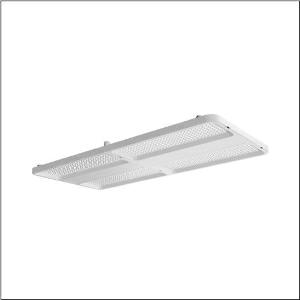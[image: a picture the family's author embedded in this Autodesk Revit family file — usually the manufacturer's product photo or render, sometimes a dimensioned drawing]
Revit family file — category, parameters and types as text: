
# Revit family: highbay_21_maxi_52hn11db4qda02
name_source: partatom
category: Lighting Fixtures
units: mm (PartAtom-declared; Revit-internal decimal feet)

## family parameters
Cut with Voids When Loaded = No
Host = Face
Light Source = No
Part Type = Normal
Room Calculation Point = No
Round Connector Dimension = Use Diameter
Shared = No

## types (1)
- --- (1 x LED, 38000 lm, 198.2 W, 4000K)
    Apparent Load = 198 VA
    CIE Flux Codes = 89 97 99 100 100
    Color Rendering = 80
    Color Temperature = 4000K
    Default Elevation = 1800 mm
    Description = high bay luminaire Highbay 21 maxi; direct symmetric narrow distribution, light control with lens of PMMA; UGR ≤ 19 (X = 4H | Y = 8H | S = 0.25H | reflection values 70/50/20); luminous flux: 38.000lm; light colour: 840, colour temperature: 4000K, MacAdam ≤ 3 SDCM (initial), colour rendering: CRI > 80; luminous efficacy: 191,7lm/W; rated service life: 75.000h (L80) at AT= ta max; control: Bluetooth Mesh; for wireless networking: Node luminaire for setting up a local control solution without a higher-level application controller, intelligence completely in the luminaire; no control line such as DALI between the Node multi-sensor luminaires and Nodes is required, wireless integration of other Node luminaires and Node multi-sensor luminaires into the network is possible; number of Node luminaires in the project can be expanded as required, network sizes > 300 Nodes can be realized; can also be connected to lighting or building automation via various gateways upon request; integrated DALI2 ECG provides luminaire data (according to IEC62386, Part 251), energy data (Part 252), and monitoring and analytics data (Part 253) to higher-level systems for further processing; luminaire connection: terminal, 5-pole, max. 2.5mm² (cable entry for one cable, Ø 8.5..16mm); mains connection: 230..240V, AC 50/60Hz; connected load: 198,2W; protection rating (complete): IP66; insulation class (complete): insulation class I (protective earthing); protection symbol: D; impact resistance: IK08; certification: CE, UKCA; internal wiring halogen-free; luminaire LABS conformity tested according to VDMA 24364:2018-05; Suitable for use in the food industry according to the specifications of IFS-Food, HACCP and/or BRC; housing frame of high-performance plastic PA6, matt traffic white (RAL 9016); cover of PMMA; dimension (LxWxH): 946 x 442 x 72mm; permissible operating ambient temperature: -20..+40°C (reducing of maximum allowable ambient temperature of 5°C with ceiling mounting); packaging unit: 1 piece; (delivery without accessories; please order mounting accessories separately)
    Height = 72 mm  [stored 0.23622 ft]
    Lamp = 1 x LED
    Lamp Light Flux = 38000 lm
    Lamp Power = 198.2 W
    Lamp count = 1
    Length = 946 mm
    Luminous efficacy = 192 lm/W
    Manufacturer = Siteco
    ModVariant = No
    Model = 52HN11DB4QDA02
    Mounting Place = Ceiling
    Mounting Type = Pendant
    Number of Poles = 1
    OnlyDefault = Yes
    Power Factor = 1
    Product Name = Highbay 21 maxi
    Product group = high bay luminaire
    ProductGroupID = 902
    Protection Class = Protection class I
    Protection Degree = IP 66
    RLX_Detail_Level = 1
    RLX_Emergency_Light_Flux = 0 lm
    RLX_Emergency_Type = 0
    RLX_Emergency_Type_DB = No
    RlxData = <blob elided: 128609 chars, md5=8ff6dd8f>
    Socket = socket
    Standby Power = 0 W
    System Light Flux = 38001 lm
    System Power = 198 W
    Type Comments = factory setting: luminous flux: 100 % | dim-lin: 254 | 918 mA
    Type Image = l_1363244.jpg
    URL = http://relux.com
    VarID = @adj_012491
    Voltage = 0 V
    Weight = 0.00 kg
    Width = 442 mm

note: [stored X ft] marks values corroborated as IEEE doubles in the binary element streams (Revit-internal decimal feet)

## geometry (parser evidence)
native form markers: Blend x4, Sweep x10
no freeform markers — native parametric forms only
